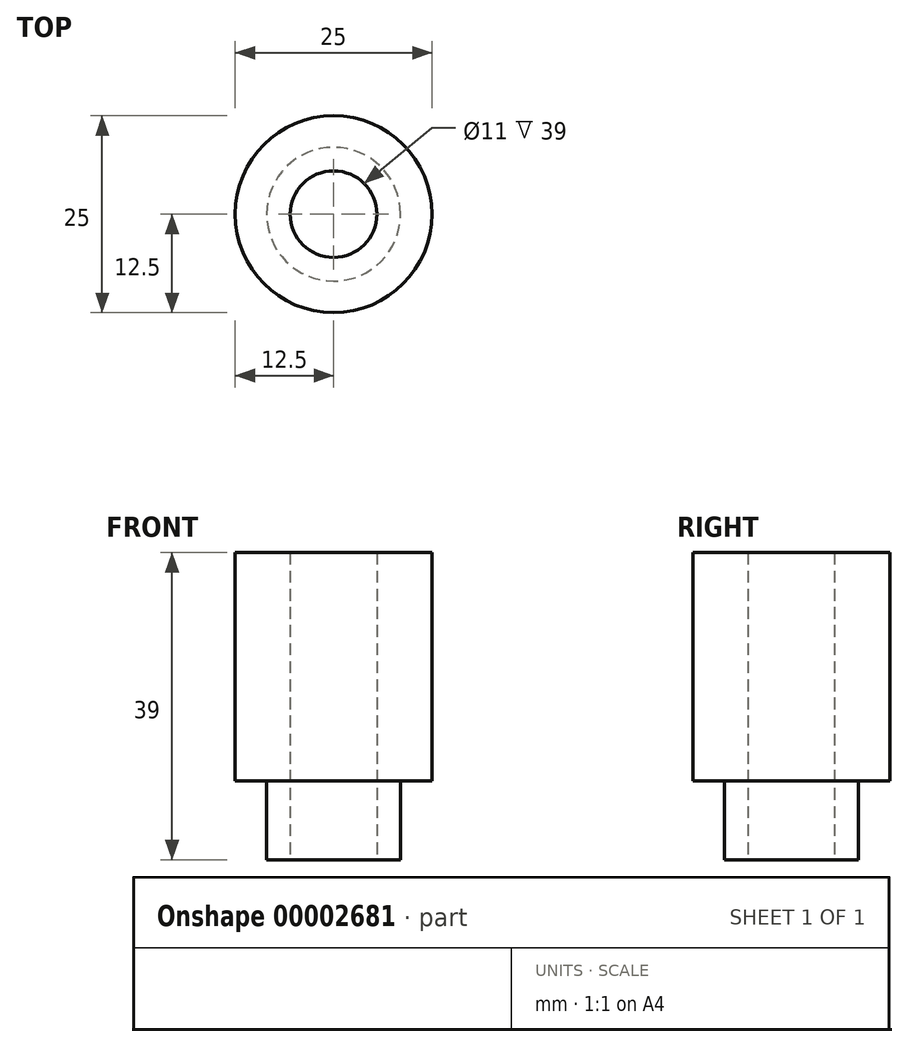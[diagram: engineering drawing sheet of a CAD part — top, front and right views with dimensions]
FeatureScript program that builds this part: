
annotation { "Feature Type Name" : "Feature", "Feature Type Description" : "" }
export const myFeature = defineFeature(function(context is Context, id is Id, definition is map)
    precondition{}
    {
        {
            var Q0;
            Q0=qCreatedBy(makeId("Top.planeOp"),FACE);
            var sketch = newSketch(context, id + "F0", { "sketchPlane" : qUnion([Q0])});
            skCircle(sketch, "E0", {"center": v(0, 0) * mm, "radius": 12.5 * mm});
            skCircle(sketch, "E1", {"center": v(0, 0) * mm, "radius": 5.5 * mm});
            skSolve(sketch);
        }
        {
            var Q0;
            Q0 = qSketchRegion(id + "F0", true);
            extrude(context, id + "F1", {"entities" : qUnion([Q0]), "depth" : 39 * mm});
        }
        {
            var Q0;
            Q0=makeQuery(id+"F1.opExtrude","CAP_FACE",FACE,{"disambiguationData":[OSD([sQuery(id+"F0.wireOp",EDGE,"E0"),sQuery(id+"F0.wireOp",EDGE,"E1")])],"isStart":true});
            var sketch = newSketch(context, id + "F2", { "sketchPlane" : qUnion([Q0])});
            skCircle(sketch, "E2", {"center": v(0, 0) * mm, "radius": 8.5 * mm});
            skSolve(sketch);
        }
        {
            var Q0;
            Q0=makeQuery(id+"F2.imprint","IMPRINT",FACE,{"disambiguationData":[TD([[makeQuery(id+"F2.imprint","IMPRINT",EDGE,{"derivedFrom":sQuery(id+"F2.wireOp",EDGE,"E2")}),-1.0]])]});
            extrude(context, id + "F3", {"entities" : qUnion([Q0]), "operationType" : NewBodyOperationType.REMOVE, "oppositeDirection" : true, "depth" : 10 * mm});
        }
    });
